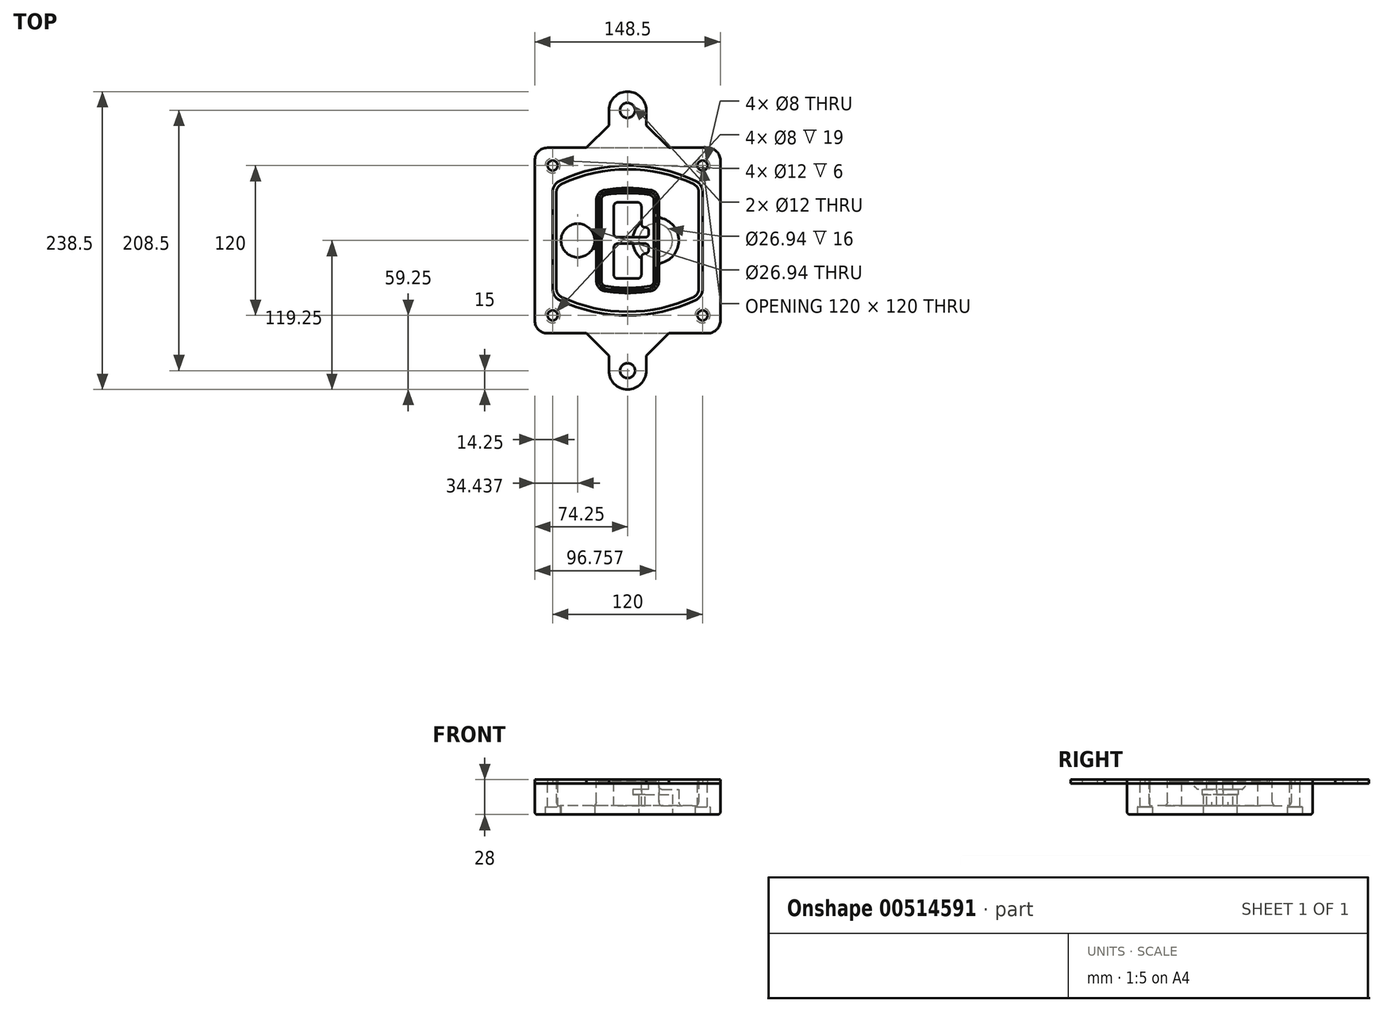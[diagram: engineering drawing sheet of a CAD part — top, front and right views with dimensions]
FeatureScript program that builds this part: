
annotation { "Feature Type Name" : "Feature", "Feature Type Description" : "" }
export const myFeature = defineFeature(function(context is Context, id is Id, definition is map)
    precondition{}
    {
        {
            var Q0;
            Q0=qCreatedBy(makeId("Top.planeOp"),FACE);
            var sketch = newSketch(context, id + "F0", { "sketchPlane" : qUnion([Q0])});
            skPoint(sketch, "E0.rect.middle", {"position": v(0, 0) * mm});
            skLineSegment(sketch, "E1.bottom", {"start": v(-64.25, -74.25) * mm, "end": v(64.25, -74.25) * mm});
            skLineSegment(sketch, "E1.top", {"start": v(-64.25, 74.25) * mm, "end": v(64.25, 74.25) * mm});
            skLineSegment(sketch, "E1.left", {"start": v(-74.25, -64.25) * mm, "end": v(-74.25, 64.25) * mm});
            skLineSegment(sketch, "E1.right", {"start": v(74.25, -64.25) * mm, "end": v(74.25, 64.25) * mm});
            skLineSegment(sketch, "E2", {"start": v(-74.25, 74.25) * mm, "end": v(74.25, -74.25) * mm, "construction": true});
            skLineSegment(sketch, "E3", {"start": v(74.25, 74.25) * mm, "end": v(-74.25, -74.25) * mm, "construction": true});
            skCircle(sketch, "E4", {"center": v(-60, 60) * mm, "radius": 4 * mm});
            skCircle(sketch, "E5", {"center": v(60, 60) * mm, "radius": 4 * mm});
            skCircle(sketch, "E6", {"center": v(60, -60) * mm, "radius": 4 * mm});
            skCircle(sketch, "E7", {"center": v(-60, -60) * mm, "radius": 4 * mm});
            skLineSegment(sketch, "E8", {"start": v(-60, 60) * mm, "end": v(60, 60) * mm, "construction": true});
            skLineSegment(sketch, "E9", {"start": v(60, 60) * mm, "end": v(60, -60) * mm, "construction": true});
            skLineSegment(sketch, "E10", {"start": v(60, -60) * mm, "end": v(-60, -60) * mm, "construction": true});
            skLineSegment(sketch, "E11", {"start": v(-60, -60) * mm, "end": v(-60, 60) * mm, "construction": true});
            skLineSegment(sketch, "E12", {"start": v(-60, 38.83) * mm, "end": v(-60, -38.83) * mm});
            skLineSegment(sketch, "E13", {"start": v(60, 38.83) * mm, "end": v(60, -38.83) * mm});
            skArc(sketch, "E14", {"start": v(54.26, 47.88) * mm, "mid": v(0, 60) * mm, "end": v(-54.26, 47.88) * mm});
            skArc(sketch, "E15", {"start": v(-54.26, -47.88) * mm, "mid": v(0, -60) * mm, "end": v(54.26, -47.88) * mm});
            skLineSegment(sketch, "E16", {"start": v(-60, 0) * mm, "end": v(60, 0) * mm, "construction": true});
            skPoint(sketch, "E17.visualSharp", {"position": v(-60, -45) * mm});
            skArc(sketch, "E17.filletArc", {"start": v(-60, -38.83) * mm, "mid": v(-58.44, -44.2) * mm, "end": v(-54.26, -47.88) * mm});
            skPoint(sketch, "E18.visualSharp", {"position": v(-60, 45) * mm});
            skArc(sketch, "E18.filletArc", {"start": v(-54.26, 47.88) * mm, "mid": v(-58.44, 44.2) * mm, "end": v(-60, 38.83) * mm});
            skPoint(sketch, "E19.visualSharp", {"position": v(60, 45) * mm});
            skArc(sketch, "E19.filletArc", {"start": v(60, 38.83) * mm, "mid": v(58.44, 44.2) * mm, "end": v(54.26, 47.88) * mm});
            skPoint(sketch, "E20.visualSharp", {"position": v(60, -45) * mm});
            skArc(sketch, "E20.filletArc", {"start": v(54.26, -47.88) * mm, "mid": v(58.44, -44.2) * mm, "end": v(60, -38.83) * mm});
            skPoint(sketch, "E21.visualSharp", {"position": v(-74.25, 74.25) * mm});
            skArc(sketch, "E21.filletArc", {"start": v(-64.25, 74.25) * mm, "mid": v(-71.32, 71.32) * mm, "end": v(-74.25, 64.25) * mm});
            skPoint(sketch, "E22.visualSharp", {"position": v(74.25, 74.25) * mm});
            skArc(sketch, "E22.filletArc", {"start": v(74.25, 64.25) * mm, "mid": v(71.32, 71.32) * mm, "end": v(64.25, 74.25) * mm});
            skPoint(sketch, "E23.visualSharp", {"position": v(74.25, -74.25) * mm});
            skArc(sketch, "E23.filletArc", {"start": v(64.25, -74.25) * mm, "mid": v(71.32, -71.32) * mm, "end": v(74.25, -64.25) * mm});
            skPoint(sketch, "E24.visualSharp", {"position": v(-74.25, -74.25) * mm});
            skArc(sketch, "E24.filletArc", {"start": v(-74.25, -64.25) * mm, "mid": v(-71.32, -71.32) * mm, "end": v(-64.25, -74.25) * mm});
            skArc(sketch, "E25.0", {"start": v(57, 38.83) * mm, "mid": v(55.9, 42.58) * mm, "end": v(52.98, 45.17) * mm});
            skLineSegment(sketch, "E25.1", {"start": v(57, 38.83) * mm, "end": v(57, -38.83) * mm});
            skArc(sketch, "E25.2", {"start": v(52.98, -45.17) * mm, "mid": v(55.9, -42.58) * mm, "end": v(57, -38.83) * mm});
            skArc(sketch, "E25.3", {"start": v(-52.98, -45.17) * mm, "mid": v(0, -57) * mm, "end": v(52.98, -45.17) * mm});
            skArc(sketch, "E25.4", {"start": v(-57, -38.83) * mm, "mid": v(-55.9, -42.58) * mm, "end": v(-52.98, -45.17) * mm});
            skArc(sketch, "E25.5", {"start": v(52.98, 45.17) * mm, "mid": v(0, 57) * mm, "end": v(-52.98, 45.17) * mm});
            skLineSegment(sketch, "E25.6", {"start": v(-57, 38.83) * mm, "end": v(-57, -38.83) * mm});
            skArc(sketch, "E25.7", {"start": v(-52.98, 45.17) * mm, "mid": v(-55.9, 42.58) * mm, "end": v(-57, 38.83) * mm});
            skArc(sketch, "E26.0", {"start": v(-55.96, 51.5) * mm, "mid": v(-61.82, 46.33) * mm, "end": v(-64, 38.83) * mm});
            skArc(sketch, "E26.1", {"start": v(55.96, 51.5) * mm, "mid": v(0, 64) * mm, "end": v(-55.96, 51.5) * mm});
            skArc(sketch, "E26.2", {"start": v(64, 38.83) * mm, "mid": v(61.82, 46.33) * mm, "end": v(55.96, 51.5) * mm});
            skLineSegment(sketch, "E26.3", {"start": v(64, 38.83) * mm, "end": v(64, -38.83) * mm});
            skArc(sketch, "E26.4", {"start": v(55.96, -51.5) * mm, "mid": v(61.82, -46.33) * mm, "end": v(64, -38.83) * mm});
            skLineSegment(sketch, "E26.5", {"start": v(-64, 38.83) * mm, "end": v(-64, -38.83) * mm});
            skArc(sketch, "E26.6", {"start": v(-55.96, -51.5) * mm, "mid": v(0, -64) * mm, "end": v(55.96, -51.5) * mm});
            skArc(sketch, "E26.7", {"start": v(-64, -38.83) * mm, "mid": v(-61.82, -46.33) * mm, "end": v(-55.96, -51.5) * mm});
            skSolve(sketch);
        }
        {
            var Q0;
            Q0=makeQuery(id+"F0.imprint","IMPRINT",FACE,{"disambiguationData":[TD([[makeQuery(id+"F0.imprint","IMPRINT",EDGE,{"derivedFrom":sQuery(id+"F0.wireOp",EDGE,"E1.bottom")}),1.0]])]});
            var Q1;
            Q1=makeQuery(id+"F0.imprint","IMPRINT",FACE,{"disambiguationData":[TD([[makeQuery(id+"F0.imprint","IMPRINT",EDGE,{"derivedFrom":sQuery(id+"F0.wireOp",EDGE,"E12")}),1.0]])]});
            var Q2;
            Q2=makeQuery(id+"F0.imprint","IMPRINT",FACE,{"disambiguationData":[TD([[makeQuery(id+"F0.imprint","IMPRINT",EDGE,{"derivedFrom":sQuery(id+"F0.wireOp",EDGE,"E25.0")}),1.0]])]});
            var Q3;
            Q3=makeQuery(id+"F0.imprint","IMPRINT",FACE,{"disambiguationData":[TD([[makeQuery(id+"F0.imprint","IMPRINT",EDGE,{"derivedFrom":sQuery(id+"F0.wireOp",EDGE,"E12")}),-1.0]])]});
            extrude(context, id + "F1", {"entities" : qUnion([Q0, Q1, Q2, Q3]), "oppositeDirection" : true, "depth" : 25 * mm});
        }
        {
            var Q0;
            Q0=makeQuery(id+"F0.imprint","IMPRINT",FACE,{"disambiguationData":[TD([[makeQuery(id+"F0.imprint","IMPRINT",EDGE,{"derivedFrom":sQuery(id+"F0.wireOp",EDGE,"E12")}),1.0]])]});
            extrude(context, id + "F2", {"entities" : qUnion([Q0]), "operationType" : NewBodyOperationType.ADD, "depth" : 3 * mm, "offsetDistance" : 25 * mm});
        }
        {
            var Q0;
            Q0=makeQuery(id+"F0.imprint","IMPRINT",FACE,{"disambiguationData":[TD([[makeQuery(id+"F0.imprint","IMPRINT",EDGE,{"derivedFrom":sQuery(id+"F0.wireOp",EDGE,"E25.0")}),1.0]])]});
            extrude(context, id + "F3", {"entities" : qUnion([Q0]), "operationType" : NewBodyOperationType.REMOVE, "oppositeDirection" : true, "depth" : 18 * mm});
        }
        {
            var Q0;
            Q0=makeQuery(id+"F2.opExtrude","CAP_FACE",FACE,{"disambiguationData":[OSD([sQuery(id+"F0.wireOp",EDGE,"E12"),sQuery(id+"F0.wireOp",EDGE,"E13"),sQuery(id+"F0.wireOp",EDGE,"E14"),sQuery(id+"F0.wireOp",EDGE,"E15"),sQuery(id+"F0.wireOp",EDGE,"E17.filletArc"),sQuery(id+"F0.wireOp",EDGE,"E18.filletArc"),sQuery(id+"F0.wireOp",EDGE,"E19.filletArc"),sQuery(id+"F0.wireOp",EDGE,"E20.filletArc"),sQuery(id+"F0.wireOp",EDGE,"E25.0"),sQuery(id+"F0.wireOp",EDGE,"E25.1"),sQuery(id+"F0.wireOp",EDGE,"E25.2"),sQuery(id+"F0.wireOp",EDGE,"E25.3"),sQuery(id+"F0.wireOp",EDGE,"E25.4"),sQuery(id+"F0.wireOp",EDGE,"E25.5"),sQuery(id+"F0.wireOp",EDGE,"E25.6"),sQuery(id+"F0.wireOp",EDGE,"E25.7")])],"isStart":false});
            var sketch = newSketch(context, id + "F4", { "sketchPlane" : qUnion([Q0])});
            skArc(sketch, "E27.0", {"start": v(-18.34, -40.45) * mm, "mid": v(0, -42) * mm, "end": v(18.34, -40.45) * mm});
            skArc(sketch, "E28.0", {"start": v(18.34, 40.45) * mm, "mid": v(0, 42) * mm, "end": v(-18.34, 40.45) * mm});
            skLineSegment(sketch, "E29", {"start": v(-25, 32.57) * mm, "end": v(-25, -32.57) * mm});
            skLineSegment(sketch, "E30", {"start": v(25, 32.57) * mm, "end": v(25, -32.57) * mm});
            skLineSegment(sketch, "E31", {"start": v(-25, 39.1) * mm, "end": v(25, 39.1) * mm, "construction": true});
            skLineSegment(sketch, "E32", {"start": v(-25, -39.1) * mm, "end": v(25, -39.1) * mm, "construction": true});
            skPoint(sketch, "E33.visualSharp", {"position": v(-25, 39.1) * mm});
            skArc(sketch, "E33.filletArc", {"start": v(-18.34, 40.45) * mm, "mid": v(-23.11, 37.73) * mm, "end": v(-25, 32.57) * mm});
            skPoint(sketch, "E34.visualSharp", {"position": v(25, 39.1) * mm});
            skArc(sketch, "E34.filletArc", {"start": v(25, 32.57) * mm, "mid": v(23.11, 37.73) * mm, "end": v(18.34, 40.45) * mm});
            skPoint(sketch, "E35.visualSharp", {"position": v(25, -39.1) * mm});
            skArc(sketch, "E35.filletArc", {"start": v(18.34, -40.45) * mm, "mid": v(23.11, -37.73) * mm, "end": v(25, -32.57) * mm});
            skPoint(sketch, "E36.visualSharp", {"position": v(-25, -39.1) * mm});
            skArc(sketch, "E36.filletArc", {"start": v(-25, -32.57) * mm, "mid": v(-23.11, -37.73) * mm, "end": v(-18.34, -40.45) * mm});
            skArc(sketch, "E37.0", {"start": v(52.98, 45.17) * mm, "mid": v(0, 57) * mm, "end": v(-52.98, 45.17) * mm});
            skArc(sketch, "E37.1", {"start": v(-52.98, 45.17) * mm, "mid": v(-55.9, 42.58) * mm, "end": v(-57, 38.83) * mm});
            skLineSegment(sketch, "E37.2", {"start": v(-57, 38.83) * mm, "end": v(-57, -38.83) * mm});
            skArc(sketch, "E37.3", {"start": v(-57, -38.83) * mm, "mid": v(-55.9, -42.58) * mm, "end": v(-52.98, -45.17) * mm});
            skArc(sketch, "E37.4", {"start": v(-52.98, -45.17) * mm, "mid": v(0, -57) * mm, "end": v(52.98, -45.17) * mm});
            skArc(sketch, "E37.5", {"start": v(52.98, -45.17) * mm, "mid": v(55.9, -42.58) * mm, "end": v(57, -38.83) * mm});
            skLineSegment(sketch, "E37.6", {"start": v(57, 38.83) * mm, "end": v(57, -38.83) * mm});
            skArc(sketch, "E37.7", {"start": v(57, 38.83) * mm, "mid": v(55.9, 42.58) * mm, "end": v(52.98, 45.17) * mm});
            skLineSegment(sketch, "E38.0", {"start": v(23, 32.57) * mm, "end": v(23, -32.57) * mm});
            skArc(sketch, "E38.1", {"start": v(18, -38.48) * mm, "mid": v(21.58, -36.44) * mm, "end": v(23, -32.57) * mm});
            skArc(sketch, "E38.2", {"start": v(-18, -38.48) * mm, "mid": v(0, -40) * mm, "end": v(18, -38.48) * mm});
            skArc(sketch, "E38.3", {"start": v(-23, -32.57) * mm, "mid": v(-21.58, -36.44) * mm, "end": v(-18, -38.48) * mm});
            skLineSegment(sketch, "E38.4", {"start": v(-23, 32.57) * mm, "end": v(-23, -32.57) * mm});
            skArc(sketch, "E38.5", {"start": v(23, 32.57) * mm, "mid": v(21.58, 36.44) * mm, "end": v(18, 38.48) * mm});
            skArc(sketch, "E38.6", {"start": v(-18, 38.48) * mm, "mid": v(-21.58, 36.44) * mm, "end": v(-23, 32.57) * mm});
            skArc(sketch, "E38.7", {"start": v(18, 38.48) * mm, "mid": v(0, 40) * mm, "end": v(-18, 38.48) * mm});
            skArc(sketch, "E39.0", {"start": v(21, 32.57) * mm, "mid": v(20.06, 35.15) * mm, "end": v(17.67, 36.5) * mm});
            skLineSegment(sketch, "E39.1", {"start": v(21, 32.57) * mm, "end": v(21, -32.57) * mm});
            skArc(sketch, "E39.2", {"start": v(17.67, -36.5) * mm, "mid": v(20.06, -35.15) * mm, "end": v(21, -32.57) * mm});
            skArc(sketch, "E39.3", {"start": v(-17.67, -36.5) * mm, "mid": v(0, -38) * mm, "end": v(17.67, -36.5) * mm});
            skArc(sketch, "E39.4", {"start": v(-21, -32.57) * mm, "mid": v(-20.06, -35.15) * mm, "end": v(-17.67, -36.5) * mm});
            skArc(sketch, "E39.5", {"start": v(17.67, 36.5) * mm, "mid": v(0, 38) * mm, "end": v(-17.67, 36.5) * mm});
            skLineSegment(sketch, "E39.6", {"start": v(-21, 32.57) * mm, "end": v(-21, -32.57) * mm});
            skArc(sketch, "E39.7", {"start": v(-17.67, 36.5) * mm, "mid": v(-20.06, 35.15) * mm, "end": v(-21, 32.57) * mm});
            skLineSegment(sketch, "E40", {"start": v(-25, 0) * mm, "end": v(25, 0) * mm, "construction": true});
            skLineSegment(sketch, "E41", {"start": v(-11, 5.5) * mm, "end": v(-11, 27.5) * mm});
            skLineSegment(sketch, "E42", {"start": v(-8, 30.5) * mm, "end": v(8, 30.5) * mm});
            skLineSegment(sketch, "E43", {"start": v(11, 27.5) * mm, "end": v(11, 13.5) * mm});
            skLineSegment(sketch, "E44", {"start": v(14, 10.5) * mm, "end": v(14, 10.5) * mm});
            skLineSegment(sketch, "E45", {"start": v(17, 7.5) * mm, "end": v(17, 5.5) * mm});
            skLineSegment(sketch, "E46", {"start": v(14, 2.5) * mm, "end": v(-8, 2.5) * mm});
            skPoint(sketch, "E47.visualSharp", {"position": v(-11, 30.5) * mm});
            skArc(sketch, "E47.filletArc", {"start": v(-8, 30.5) * mm, "mid": v(-10.12, 29.62) * mm, "end": v(-11, 27.5) * mm});
            skPoint(sketch, "E48.visualSharp", {"position": v(11, 30.5) * mm});
            skArc(sketch, "E48.filletArc", {"start": v(11, 27.5) * mm, "mid": v(10.12, 29.62) * mm, "end": v(8, 30.5) * mm});
            skPoint(sketch, "E49.visualSharp", {"position": v(11, 10.5) * mm});
            skArc(sketch, "E49.filletArc", {"start": v(11, 13.5) * mm, "mid": v(11.88, 11.38) * mm, "end": v(14, 10.5) * mm});
            skPoint(sketch, "E50.visualSharp", {"position": v(17, 10.5) * mm});
            skArc(sketch, "E50.filletArc", {"start": v(17, 7.5) * mm, "mid": v(16.12, 9.62) * mm, "end": v(14, 10.5) * mm});
            skPoint(sketch, "E51.visualSharp", {"position": v(17, 2.5) * mm});
            skArc(sketch, "E51.filletArc", {"start": v(14, 2.5) * mm, "mid": v(16.12, 3.38) * mm, "end": v(17, 5.5) * mm});
            skPoint(sketch, "E52.visualSharp", {"position": v(-11, 2.5) * mm});
            skArc(sketch, "E52.filletArc", {"start": v(-11, 5.5) * mm, "mid": v(-10.12, 3.38) * mm, "end": v(-8, 2.5) * mm});
            skLineSegment(sketch, "E53.0.MirrorCS", {"start": v(14, -2.5) * mm, "end": v(-8, -2.5) * mm});
            skArc(sketch, "E54.0.MirrorCS", {"start": v(-11, -5.5) * mm, "mid": v(-10.12, -3.38) * mm, "end": v(-8, -2.5) * mm});
            skLineSegment(sketch, "E55.0.MirrorCS", {"start": v(-11, -5.5) * mm, "end": v(-11, -27.5) * mm});
            skArc(sketch, "E56.0.MirrorCS", {"start": v(-8, -30.5) * mm, "mid": v(-10.12, -29.62) * mm, "end": v(-11, -27.5) * mm});
            skLineSegment(sketch, "E57.0.MirrorCS", {"start": v(-8, -30.5) * mm, "end": v(8, -30.5) * mm});
            skArc(sketch, "E58.0.MirrorCS", {"start": v(11, -27.5) * mm, "mid": v(10.12, -29.62) * mm, "end": v(8, -30.5) * mm});
            skLineSegment(sketch, "E59.0.MirrorCS", {"start": v(11, -27.5) * mm, "end": v(11, -13.5) * mm});
            skArc(sketch, "E60.0.MirrorCS", {"start": v(11, -13.5) * mm, "mid": v(11.88, -11.38) * mm, "end": v(14, -10.5) * mm});
            skArc(sketch, "E61.0.MirrorCS", {"start": v(17, -7.5) * mm, "mid": v(16.12, -9.62) * mm, "end": v(14, -10.5) * mm});
            skLineSegment(sketch, "E62.0.MirrorCS", {"start": v(17, -7.5) * mm, "end": v(17, -5.5) * mm});
            skArc(sketch, "E63.0.MirrorCS", {"start": v(14, -2.5) * mm, "mid": v(16.12, -3.38) * mm, "end": v(17, -5.5) * mm});
            skSolve(sketch);
        }
        {
            var Q0;
            Q0=makeQuery(id+"F4.imprint","IMPRINT",FACE,{"disambiguationData":[TD([[makeQuery(id+"F4.imprint","IMPRINT",EDGE,{"derivedFrom":sQuery(id+"F4.wireOp",EDGE,"E27.0")}),1.0]])]});
            var Q1;
            Q1=makeQuery(id+"F4.imprint","IMPRINT",FACE,{"disambiguationData":[TD([[makeQuery(id+"F4.imprint","IMPRINT",EDGE,{"derivedFrom":sQuery(id+"F4.wireOp",EDGE,"E38.0")}),-1.0]])]});
            var Q2;
            Q2=makeQuery(id+"F4.imprint","IMPRINT",FACE,{"disambiguationData":[TD([[makeQuery(id+"F4.imprint","IMPRINT",EDGE,{"derivedFrom":sQuery(id+"F4.wireOp",EDGE,"E39.0")}),1.0]])]});
            extrude(context, id + "F5", {"entities" : qUnion([Q0, Q1, Q2]), "operationType" : NewBodyOperationType.ADD, "endBound" : BoundingType.UP_TO_NEXT, "oppositeDirection" : true, "depth" : 25 * mm});
        }
        {
            var Q0;
            Q0=makeQuery(id+"F4.imprint","IMPRINT",FACE,{"disambiguationData":[TD([[makeQuery(id+"F4.imprint","IMPRINT",EDGE,{"derivedFrom":sQuery(id+"F4.wireOp",EDGE,"E38.0")}),-1.0]])]});
            extrude(context, id + "F6", {"entities" : qUnion([Q0]), "operationType" : NewBodyOperationType.REMOVE, "oppositeDirection" : true, "depth" : 2 * mm});
        }
        {
            var Q0;
            Q0=makeQuery(id+"F1.opExtrude","CAP_FACE",FACE,{"disambiguationData":[OSD([sQuery(id+"F0.wireOp",EDGE,"E1.bottom"),sQuery(id+"F0.wireOp",EDGE,"E1.top"),sQuery(id+"F0.wireOp",EDGE,"E1.left"),sQuery(id+"F0.wireOp",EDGE,"E1.right"),sQuery(id+"F0.wireOp",EDGE,"E4"),sQuery(id+"F0.wireOp",EDGE,"E5"),sQuery(id+"F0.wireOp",EDGE,"E6"),sQuery(id+"F0.wireOp",EDGE,"E7"),sQuery(id+"F0.wireOp",EDGE,"E21.filletArc"),sQuery(id+"F0.wireOp",EDGE,"E22.filletArc"),sQuery(id+"F0.wireOp",EDGE,"E23.filletArc"),sQuery(id+"F0.wireOp",EDGE,"E24.filletArc")])],"isStart":false});
            var sketch = newSketch(context, id + "F7", { "sketchPlane" : qUnion([Q0])});
            skCircle(sketch, "E64", {"center": v(22.5, 0) * mm, "radius": 13.47 * mm});
            skCircle(sketch, "E65", {"center": v(-39.81, 0) * mm, "radius": 13.47 * mm});
            skLineSegment(sketch, "E66", {"start": v(74.25, 0) * mm, "end": v(-74.25, 0) * mm});
            skCircle(sketch, "E67", {"center": v(22.5, 0) * mm, "radius": 18.47 * mm});
            skCircle(sketch, "E68", {"center": v(60, -60) * mm, "radius": 6 * mm});
            skCircle(sketch, "E69", {"center": v(-60, -60) * mm, "radius": 6 * mm});
            skCircle(sketch, "E70", {"center": v(-60, 60) * mm, "radius": 6 * mm});
            skCircle(sketch, "E71", {"center": v(60, 60) * mm, "radius": 6 * mm});
            skSolve(sketch);
        }
        {
            var Q0;
            {var subQ1=sQuery(id+"F7.wireOp",EDGE,"E66");var subQ4=sQuery(id+"F7.wireOp",EDGE,"E64");var subQ6=makeQuery(id+"F7.imprint","INTERSECT",VERTEX,{"disambiguationData":[OD(0.0)],"derivedFrom":[subQ4,subQ1]});Q0=makeQuery(id+"F7.imprint","IMPRINT",FACE,{"disambiguationData":[TD([[makeQuery(id+"F7.imprint","IMPRINT",EDGE,{"disambiguationData":[TD([[subQ6,-1.0]])],"derivedFrom":subQ4}),-1.0]])]});}
            var Q1;
            {var subQ0=sQuery(id+"F7.wireOp",EDGE,"E66");var subQ1=sQuery(id+"F7.wireOp",EDGE,"E64");var subQ3=makeQuery(id+"F7.imprint","INTERSECT",VERTEX,{"disambiguationData":[OD(0.0)],"derivedFrom":[subQ1,subQ0]});Q1=makeQuery(id+"F7.imprint","IMPRINT",FACE,{"disambiguationData":[TD([[makeQuery(id+"F7.imprint","IMPRINT",EDGE,{"disambiguationData":[TD([[subQ3,-1.0]])],"derivedFrom":subQ1}),1.0]])]});}
            var Q2;
            {var subQ0=sQuery(id+"F7.wireOp",EDGE,"E66");var subQ1=sQuery(id+"F7.wireOp",EDGE,"E64");var subQ3=makeQuery(id+"F7.imprint","INTERSECT",VERTEX,{"disambiguationData":[OD(0.0)],"derivedFrom":[subQ1,subQ0]});Q2=makeQuery(id+"F7.imprint","IMPRINT",FACE,{"disambiguationData":[TD([[makeQuery(id+"F7.imprint","IMPRINT",EDGE,{"disambiguationData":[TD([[subQ3,1.0]])],"derivedFrom":subQ1}),1.0]])]});}
            var Q3;
            {var subQ1=sQuery(id+"F7.wireOp",EDGE,"E66");var subQ4=sQuery(id+"F7.wireOp",EDGE,"E64");var subQ6=makeQuery(id+"F7.imprint","INTERSECT",VERTEX,{"disambiguationData":[OD(0.0)],"derivedFrom":[subQ4,subQ1]});Q3=makeQuery(id+"F7.imprint","IMPRINT",FACE,{"disambiguationData":[TD([[makeQuery(id+"F7.imprint","IMPRINT",EDGE,{"disambiguationData":[TD([[subQ6,1.0]])],"derivedFrom":subQ4}),-1.0]])]});}
            extrude(context, id + "F8", {"entities" : qUnion([Q0, Q1, Q2, Q3]), "operationType" : NewBodyOperationType.ADD, "oppositeDirection" : true, "depth" : 20 * mm});
        }
        {
            var Q0;
            {var subQ0=sQuery(id+"F7.wireOp",EDGE,"E66");var subQ1=sQuery(id+"F7.wireOp",EDGE,"E64");var subQ3=makeQuery(id+"F7.imprint","INTERSECT",VERTEX,{"disambiguationData":[OD(0.0)],"derivedFrom":[subQ1,subQ0]});Q0=makeQuery(id+"F7.imprint","IMPRINT",FACE,{"disambiguationData":[TD([[makeQuery(id+"F7.imprint","IMPRINT",EDGE,{"disambiguationData":[TD([[subQ3,-1.0]])],"derivedFrom":subQ1}),1.0]])]});}
            var Q1;
            {var subQ0=sQuery(id+"F7.wireOp",EDGE,"E66");var subQ1=sQuery(id+"F7.wireOp",EDGE,"E64");var subQ3=makeQuery(id+"F7.imprint","INTERSECT",VERTEX,{"disambiguationData":[OD(0.0)],"derivedFrom":[subQ1,subQ0]});Q1=makeQuery(id+"F7.imprint","IMPRINT",FACE,{"disambiguationData":[TD([[makeQuery(id+"F7.imprint","IMPRINT",EDGE,{"disambiguationData":[TD([[subQ3,1.0]])],"derivedFrom":subQ1}),1.0]])]});}
            extrude(context, id + "F9", {"entities" : qUnion([Q0, Q1]), "operationType" : NewBodyOperationType.REMOVE, "oppositeDirection" : true, "depth" : 16 * mm});
        }
        {
            var Q0;
            {var subQ0=sQuery(id+"F7.wireOp",EDGE,"E66");var subQ1=sQuery(id+"F7.wireOp",EDGE,"E65");var subQ3=makeQuery(id+"F7.imprint","INTERSECT",VERTEX,{"disambiguationData":[OD(0.0)],"derivedFrom":[subQ1,subQ0]});Q0=makeQuery(id+"F7.imprint","IMPRINT",FACE,{"disambiguationData":[TD([[makeQuery(id+"F7.imprint","IMPRINT",EDGE,{"disambiguationData":[TD([[subQ3,-1.0]])],"derivedFrom":subQ1}),1.0]])]});}
            var Q1;
            {var subQ0=sQuery(id+"F7.wireOp",EDGE,"E66");var subQ1=sQuery(id+"F7.wireOp",EDGE,"E65");var subQ3=makeQuery(id+"F7.imprint","INTERSECT",VERTEX,{"disambiguationData":[OD(0.0)],"derivedFrom":[subQ1,subQ0]});Q1=makeQuery(id+"F7.imprint","IMPRINT",FACE,{"disambiguationData":[TD([[makeQuery(id+"F7.imprint","IMPRINT",EDGE,{"disambiguationData":[TD([[subQ3,1.0]])],"derivedFrom":subQ1}),1.0]])]});}
            extrude(context, id + "F10", {"entities" : qUnion([Q0, Q1]), "operationType" : NewBodyOperationType.REMOVE, "oppositeDirection" : true, "depth" : 25 * mm});
        }
        {
            var Q0;
            Q0=makeQuery(id+"F7.imprint","IMPRINT",FACE,{"disambiguationData":[TD([[makeQuery(id+"F7.imprint","IMPRINT",EDGE,{"derivedFrom":sQuery(id+"F7.wireOp",EDGE,"E68")}),1.0]])]});
            var Q1;
            Q1=makeQuery(id+"F7.imprint","IMPRINT",FACE,{"disambiguationData":[TD([[makeQuery(id+"F7.imprint","IMPRINT",EDGE,{"derivedFrom":makeQuery(id+"F1.opExtrude","CAP_EDGE",EDGE,{"disambiguationData":[OSD([sQuery(id+"F0.wireOp",EDGE,"E5")])],"isStart":false})}),-1.0]])]});
            var Q2;
            Q2=makeQuery(id+"F7.imprint","IMPRINT",FACE,{"disambiguationData":[TD([[makeQuery(id+"F7.imprint","IMPRINT",EDGE,{"derivedFrom":sQuery(id+"F7.wireOp",EDGE,"E69")}),1.0]])]});
            var Q3;
            Q3=makeQuery(id+"F7.imprint","IMPRINT",FACE,{"disambiguationData":[TD([[makeQuery(id+"F7.imprint","IMPRINT",EDGE,{"derivedFrom":makeQuery(id+"F1.opExtrude","CAP_EDGE",EDGE,{"disambiguationData":[OSD([sQuery(id+"F0.wireOp",EDGE,"E4")])],"isStart":false})}),-1.0]])]});
            var Q4;
            Q4=makeQuery(id+"F7.imprint","IMPRINT",FACE,{"disambiguationData":[TD([[makeQuery(id+"F7.imprint","IMPRINT",EDGE,{"derivedFrom":sQuery(id+"F7.wireOp",EDGE,"E70")}),1.0]])]});
            var Q5;
            Q5=makeQuery(id+"F7.imprint","IMPRINT",FACE,{"disambiguationData":[TD([[makeQuery(id+"F7.imprint","IMPRINT",EDGE,{"derivedFrom":makeQuery(id+"F1.opExtrude","CAP_EDGE",EDGE,{"disambiguationData":[OSD([sQuery(id+"F0.wireOp",EDGE,"E7")])],"isStart":false})}),-1.0]])]});
            var Q6;
            Q6=makeQuery(id+"F7.imprint","IMPRINT",FACE,{"disambiguationData":[TD([[makeQuery(id+"F7.imprint","IMPRINT",EDGE,{"derivedFrom":sQuery(id+"F7.wireOp",EDGE,"E71")}),1.0]])]});
            var Q7;
            Q7=makeQuery(id+"F7.imprint","IMPRINT",FACE,{"disambiguationData":[TD([[makeQuery(id+"F7.imprint","IMPRINT",EDGE,{"derivedFrom":makeQuery(id+"F1.opExtrude","CAP_EDGE",EDGE,{"disambiguationData":[OSD([sQuery(id+"F0.wireOp",EDGE,"E6")])],"isStart":false})}),-1.0]])]});
            extrude(context, id + "F11", {"entities" : qUnion([Q0, Q1, Q2, Q3, Q4, Q5, Q6, Q7]), "operationType" : NewBodyOperationType.REMOVE, "oppositeDirection" : true, "depth" : 6 * mm});
        }
        {
            var Q0;
            Q0=makeQuery(id+"F9.boolean.opBoolean","COPY",FACE,{"derivedFrom":makeQuery(id+"F9.opExtrude","CAP_FACE",FACE,{"disambiguationData":[OSD([sQuery(id+"F7.wireOp",EDGE,"E64")])],"isStart":false})});
            var sketch = newSketch(context, id + "F12", { "sketchPlane" : qUnion([Q0])});
            skArc(sketch, "E72.0", {"start": v(11, 14.45) * mm, "mid": v(6.45, 9.13) * mm, "end": v(4.2, 2.5) * mm});
            skArc(sketch, "E72.1", {"start": v(4.2, -2.5) * mm, "mid": v(6.45, -9.13) * mm, "end": v(11, -14.45) * mm});
            skLineSegment(sketch, "E73", {"start": v(4.2, -2.5) * mm, "end": v(14, -2.5) * mm});
            skLineSegment(sketch, "E74.0", {"start": v(14, 2.5) * mm, "end": v(4.2, 2.5) * mm});
            skArc(sketch, "E74.1", {"start": v(14, 2.5) * mm, "mid": v(16.12, 3.38) * mm, "end": v(17, 5.5) * mm});
            skLineSegment(sketch, "E74.2", {"start": v(17, 7.5) * mm, "end": v(17, 5.5) * mm});
            skArc(sketch, "E74.3", {"start": v(17, 7.5) * mm, "mid": v(16.12, 9.62) * mm, "end": v(14, 10.5) * mm});
            skArc(sketch, "E74.4", {"start": v(11, 13.5) * mm, "mid": v(11.88, 11.38) * mm, "end": v(14, 10.5) * mm});
            skLineSegment(sketch, "E74.5", {"start": v(11, 14.45) * mm, "end": v(11, 13.5) * mm});
            skLineSegment(sketch, "E74.7", {"start": v(14, -2.5) * mm, "end": v(4.2, -2.5) * mm});
            skArc(sketch, "E74.8", {"start": v(14, -2.5) * mm, "mid": v(16.12, -3.38) * mm, "end": v(17, -5.5) * mm});
            skLineSegment(sketch, "E74.9", {"start": v(17, -7.5) * mm, "end": v(17, -5.5) * mm});
            skArc(sketch, "E74.10", {"start": v(17, -7.5) * mm, "mid": v(16.12, -9.62) * mm, "end": v(14, -10.5) * mm});
            skArc(sketch, "E74.11", {"start": v(11, -13.5) * mm, "mid": v(11.88, -11.38) * mm, "end": v(14, -10.5) * mm});
            skLineSegment(sketch, "E74.12", {"start": v(11, -14.45) * mm, "end": v(11, -13.5) * mm});
            skPoint(sketch, "E75.orphan", {"position": v(11, -27.5) * mm});
            skPoint(sketch, "E76.orphan", {"position": v(-8, -2.5) * mm});
            skPoint(sketch, "E77.orphan", {"position": v(-8, 2.5) * mm});
            skPoint(sketch, "E78.orphan", {"position": v(11, 27.5) * mm});
            skSolve(sketch);
        }
        {
            var Q0;
            {var subQ7=sQuery(id+"F12.wireOp",EDGE,"E72.0");var subQ14=sQuery(id+"F12.wireOp",EDGE,"E72.1");var subQ16=sQuery(id+"F12.wireOp",EDGE,"E74.1");var subQ18=sQuery(id+"F12.wireOp",EDGE,"E74.8");Q0=qUnion([makeQuery(id+"F12.imprint","IMPRINT",FACE,{"disambiguationData":[TD([[makeQuery(id+"F12.imprint","IMPRINT",EDGE,{"derivedFrom":subQ7}),1.0]])]}),makeQuery(id+"F12.imprint","IMPRINT",FACE,{"disambiguationData":[TD([[makeQuery(id+"F12.imprint","IMPRINT",EDGE,{"derivedFrom":subQ14}),1.0]])]}),makeQuery(id+"F12.imprint","IMPRINT",FACE,{"disambiguationData":[TD([[makeQuery(id+"F12.imprint","IMPRINT",EDGE,{"derivedFrom":subQ16}),1.0]])]}),makeQuery(id+"F12.imprint","IMPRINT",FACE,{"disambiguationData":[TD([[makeQuery(id+"F12.imprint","IMPRINT",EDGE,{"derivedFrom":subQ18}),-1.0]])]})]);}
            var Q1;
            Q1=makeQuery(id+"F5.boolean.opBoolean","SPLIT",FACE,{"disambiguationData":[TD([makeQuery(id+"F5.opExtrude","SWEPT_FACE",FACE,{"disambiguationData":[OSD([sQuery(id+"F4.wireOp",EDGE,"E41")])]})])],"derivedFrom":makeQuery(id+"F3.boolean.opBoolean","COPY",FACE,{"derivedFrom":makeQuery(id+"F3.opExtrude","CAP_FACE",FACE,{"disambiguationData":[OSD([sQuery(id+"F0.wireOp",EDGE,"E25.0"),sQuery(id+"F0.wireOp",EDGE,"E25.1"),sQuery(id+"F0.wireOp",EDGE,"E25.2"),sQuery(id+"F0.wireOp",EDGE,"E25.3"),sQuery(id+"F0.wireOp",EDGE,"E25.4"),sQuery(id+"F0.wireOp",EDGE,"E25.5"),sQuery(id+"F0.wireOp",EDGE,"E25.6"),sQuery(id+"F0.wireOp",EDGE,"E25.7")])],"isStart":false})})});
            extrude(context, id + "F13", {"entities" : qUnion([Q0]), "operationType" : NewBodyOperationType.REMOVE, "endBound" : BoundingType.UP_TO_SURFACE, "endBoundEntityFace" : qUnion([Q1]), "depth" : 25 * mm});
        }
        {
            var Q0;
            Q0=makeQuery(id+"F3.boolean.opBoolean","COPY",EDGE,{"derivedFrom":makeQuery(id+"F3.opExtrude","CAP_EDGE",EDGE,{"disambiguationData":[OSD([sQuery(id+"F0.wireOp",EDGE,"E25.6")])],"isStart":false})});
            var Q1;
            Q1=makeQuery(id+"F8.boolean.opBoolean","INTERSECT",EDGE,{"derivedFrom":[makeQuery(id+"F5.opExtrude","SWEPT_FACE",FACE,{"disambiguationData":[OSD([sQuery(id+"F4.wireOp",EDGE,"E30")])]}),makeQuery(id+"F8.opExtrude","CAP_FACE",FACE,{"disambiguationData":[OSD([sQuery(id+"F7.wireOp",EDGE,"E67")])],"isStart":false})]});
            var Q2;
            Q2=makeQuery(id+"F8.boolean.opBoolean","INTERSECT",EDGE,{"disambiguationData":[OD(1.0)],"derivedFrom":[makeQuery(id+"F5.opExtrude","SWEPT_FACE",FACE,{"disambiguationData":[OSD([sQuery(id+"F4.wireOp",EDGE,"E30")])]}),makeQuery(id+"F8.opExtrude","SWEPT_FACE",FACE,{"disambiguationData":[OSD([sQuery(id+"F7.wireOp",EDGE,"E67")])]})]});
            var Q3;
            {var subQ0=sQuery(id+"F4.wireOp",EDGE,"E30");Q3=makeQuery(id+"F8.boolean.opBoolean","SPLIT",EDGE,{"disambiguationData":[TD([makeQuery(id+"F5.opExtrude","SWEPT_FACE",FACE,{"disambiguationData":[OSD([sQuery(id+"F4.wireOp",EDGE,"E35.filletArc")])]})])],"derivedFrom":makeQuery(id+"F5.opExtrude","CAP_EDGE",EDGE,{"disambiguationData":[OSD([subQ0])],"isStart":false})});}
            var Q4;
            {var subQ0=sQuery(id+"F0.wireOp",EDGE,"E25.7");var subQ1=sQuery(id+"F0.wireOp",EDGE,"E25.1");var subQ2=sQuery(id+"F0.wireOp",EDGE,"E25.6");var subQ3=sQuery(id+"F0.wireOp",EDGE,"E25.5");var subQ4=sQuery(id+"F0.wireOp",EDGE,"E25.4");var subQ5=sQuery(id+"F0.wireOp",EDGE,"E25.0");var subQ6=sQuery(id+"F0.wireOp",EDGE,"E25.2");var subQ7=sQuery(id+"F0.wireOp",EDGE,"E25.3");Q4=makeQuery(id+"F8.boolean.opBoolean","INTERSECT",EDGE,{"derivedFrom":[makeQuery(id+"F5.boolean.opBoolean","SPLIT",FACE,{"disambiguationData":[TD([makeQuery(id+"F2.opExtrude","SWEPT_FACE",FACE,{"disambiguationData":[OSD([subQ5])]})])],"derivedFrom":makeQuery(id+"F3.boolean.opBoolean","COPY",FACE,{"derivedFrom":makeQuery(id+"F3.opExtrude","CAP_FACE",FACE,{"disambiguationData":[OSD([subQ5,subQ1,subQ6,subQ7,subQ4,subQ3,subQ2,subQ0])],"isStart":false})})}),makeQuery(id+"F8.opExtrude","SWEPT_FACE",FACE,{"disambiguationData":[OSD([sQuery(id+"F7.wireOp",EDGE,"E67")])]})]});}
            var Q5;
            Q5=makeQuery(id+"F8.boolean.opBoolean","INTERSECT",EDGE,{"disambiguationData":[OD(0.0)],"derivedFrom":[makeQuery(id+"F5.opExtrude","SWEPT_FACE",FACE,{"disambiguationData":[OSD([sQuery(id+"F4.wireOp",EDGE,"E30")])]}),makeQuery(id+"F8.opExtrude","SWEPT_FACE",FACE,{"disambiguationData":[OSD([sQuery(id+"F7.wireOp",EDGE,"E67")])]})]});
            fillet(context, id + "F14", {"entities" : qUnion([Q0, Q1, Q2, Q3, Q4, Q5]), "radius" : 3 * mm, "tangentPropagation" : true, "allowEdgeOverflow" : false});
        }
        {
            var Q0;
            Q0=makeQuery(id+"F1.opExtrude","CAP_EDGE",EDGE,{"disambiguationData":[OSD([sQuery(id+"F0.wireOp",EDGE,"E1.bottom")])],"isStart":false});
            fillet(context, id + "F15", {"entities" : qUnion([Q0]), "radius" : 2 * mm, "tangentPropagation" : true, "allowEdgeOverflow" : false});
        }
        {
            var Q0;
            {var subQ0=sQuery(id+"F0.wireOp",EDGE,"E21.filletArc");var subQ1=sQuery(id+"F0.wireOp",EDGE,"E7");var subQ2=sQuery(id+"F0.wireOp",EDGE,"E6");var subQ3=sQuery(id+"F0.wireOp",EDGE,"E5");var subQ4=sQuery(id+"F0.wireOp",EDGE,"E4");var subQ5=sQuery(id+"F0.wireOp",EDGE,"E22.filletArc");var subQ6=sQuery(id+"F0.wireOp",EDGE,"E1.bottom");var subQ7=sQuery(id+"F0.wireOp",EDGE,"E1.right");var subQ8=sQuery(id+"F0.wireOp",EDGE,"E1.top");var subQ9=sQuery(id+"F0.wireOp",EDGE,"E1.left");var subQ10=sQuery(id+"F0.wireOp",EDGE,"E23.filletArc");var subQ11=sQuery(id+"F0.wireOp",EDGE,"E24.filletArc");Q0=makeQuery(id+"F2.boolean.opBoolean","SPLIT",FACE,{"disambiguationData":[TD([makeQuery(id+"F1.opExtrude","SWEPT_FACE",FACE,{"disambiguationData":[OSD([subQ6])]})])],"derivedFrom":makeQuery(id+"F1.opExtrude","CAP_FACE",FACE,{"disambiguationData":[OSD([subQ6,subQ8,subQ9,subQ7,subQ4,subQ3,subQ2,subQ1,subQ0,subQ5,subQ10,subQ11])],"isStart":true})});}
            var sketch = newSketch(context, id + "F16", { "sketchPlane" : qUnion([Q0])});
            skArc(sketch, "E79.0", {"start": v(-64.25, 74.25) * mm, "mid": v(-71.32, 71.32) * mm, "end": v(-74.25, 64.25) * mm});
            skArc(sketch, "E79.1", {"start": v(74.25, 64.25) * mm, "mid": v(71.32, 71.32) * mm, "end": v(64.25, 74.25) * mm});
            skArc(sketch, "E79.2", {"start": v(60, 38.83) * mm, "mid": v(58.44, 44.2) * mm, "end": v(54.26, 47.88) * mm});
            skArc(sketch, "E79.3", {"start": v(-54.26, 47.88) * mm, "mid": v(-58.44, 44.2) * mm, "end": v(-60, 38.83) * mm});
            skArc(sketch, "E79.4", {"start": v(54.26, -47.88) * mm, "mid": v(58.44, -44.2) * mm, "end": v(60, -38.83) * mm});
            skArc(sketch, "E79.5", {"start": v(-60, -38.83) * mm, "mid": v(-58.44, -44.2) * mm, "end": v(-54.26, -47.88) * mm});
            skArc(sketch, "E79.6", {"start": v(64.25, -74.25) * mm, "mid": v(71.32, -71.32) * mm, "end": v(74.25, -64.25) * mm});
            skLineSegment(sketch, "E79.7", {"start": v(74.25, -64.25) * mm, "end": v(74.25, 64.25) * mm});
            skLineSegment(sketch, "E79.8", {"start": v(-64.25, 74.25) * mm, "end": v(64.25, 74.25) * mm});
            skLineSegment(sketch, "E79.9", {"start": v(-74.25, -64.25) * mm, "end": v(-74.25, 64.25) * mm});
            skArc(sketch, "E79.10", {"start": v(-74.25, -64.25) * mm, "mid": v(-71.32, -71.32) * mm, "end": v(-64.25, -74.25) * mm});
            skLineSegment(sketch, "E79.11", {"start": v(-64.25, -74.25) * mm, "end": v(64.25, -74.25) * mm});
            skLineSegment(sketch, "E79.12", {"start": v(60, 38.83) * mm, "end": v(60, -38.83) * mm});
            skArc(sketch, "E79.13", {"start": v(54.26, 47.88) * mm, "mid": v(0, 60) * mm, "end": v(-54.26, 47.88) * mm});
            skLineSegment(sketch, "E79.14", {"start": v(-60, 38.83) * mm, "end": v(-60, -38.83) * mm});
            skArc(sketch, "E79.15", {"start": v(-54.26, -47.88) * mm, "mid": v(0, -60) * mm, "end": v(54.26, -47.88) * mm});
            skCircle(sketch, "E79.16", {"center": v(60, 60) * mm, "radius": 4 * mm});
            skCircle(sketch, "E79.17", {"center": v(-60, 60) * mm, "radius": 4 * mm});
            skCircle(sketch, "E79.18", {"center": v(-60, -60) * mm, "radius": 4 * mm});
            skCircle(sketch, "E79.19", {"center": v(60, -60) * mm, "radius": 4 * mm});
            skLineSegment(sketch, "E80", {"start": v(-33, 74.25) * mm, "end": v(-15, 92.25) * mm});
            skLineSegment(sketch, "E81", {"start": v(-15, 92.25) * mm, "end": v(-15, 104.25) * mm});
            skArc(sketch, "E82", {"start": v(15, 104.25) * mm, "mid": v(0, 119.25) * mm, "end": v(-15, 104.25) * mm});
            skLineSegment(sketch, "E83", {"start": v(15, 104.25) * mm, "end": v(15, 92.25) * mm});
            skLineSegment(sketch, "E84", {"start": v(15, 92.25) * mm, "end": v(33, 74.25) * mm});
            skCircle(sketch, "E85", {"center": v(0, 104.25) * mm, "radius": 6 * mm});
            skLineSegment(sketch, "E86", {"start": v(0, 104.25) * mm, "end": v(0, 74.25) * mm, "construction": true});
            skLineSegment(sketch, "E87", {"start": v(-74.25, 0) * mm, "end": v(74.25, 0) * mm, "construction": true});
            skLineSegment(sketch, "E88.MirrorCS", {"start": v(-15, 92.25) * mm, "end": v(-33, 74.25) * mm});
            skLineSegment(sketch, "E89.MirrorCS", {"start": v(-15, 104.25) * mm, "end": v(-15, 92.25) * mm});
            skLineSegment(sketch, "E90.MirrorCS", {"start": v(33, 74.25) * mm, "end": v(15, 92.25) * mm});
            skLineSegment(sketch, "E91.MirrorCS", {"start": v(15, 92.25) * mm, "end": v(15, 104.25) * mm});
            skArc(sketch, "E92.MirrorCS", {"start": v(-15, 104.25) * mm, "mid": v(0, 119.25) * mm, "end": v(15, 104.25) * mm});
            skLineSegment(sketch, "E93.MirrorCS", {"start": v(74.25, 0) * mm, "end": v(-74.25, 0) * mm, "construction": true});
            skLineSegment(sketch, "E94.MirrorCS", {"start": v(15, -104.25) * mm, "end": v(15, -92.25) * mm});
            skLineSegment(sketch, "E95.MirrorCS", {"start": v(33, -74.25) * mm, "end": v(15, -92.25) * mm});
            skLineSegment(sketch, "E96.MirrorCS", {"start": v(-15, -92.25) * mm, "end": v(-33, -74.25) * mm});
            skLineSegment(sketch, "E97.MirrorCS", {"start": v(-15, -92.25) * mm, "end": v(-15, -104.25) * mm});
            skCircle(sketch, "E98.MirrorC", {"center": v(0, -104.25) * mm, "radius": 6 * mm});
            skLineSegment(sketch, "E99.MirrorCS", {"start": v(0, -104.25) * mm, "end": v(0, -74.25) * mm, "construction": true});
            skArc(sketch, "E100.MirrorCS", {"start": v(15, -104.25) * mm, "mid": v(0, -119.25) * mm, "end": v(-15, -104.25) * mm});
            skSolve(sketch);
        }
        {
            var Q0;
            Q0 = qSketchRegion(id + "F16", true);
            var Q1;
            Q1=makeQuery(id+"F2.opExtrude","CAP_FACE",FACE,{"disambiguationData":[OSD([sQuery(id+"F0.wireOp",EDGE,"E12"),sQuery(id+"F0.wireOp",EDGE,"E13"),sQuery(id+"F0.wireOp",EDGE,"E14"),sQuery(id+"F0.wireOp",EDGE,"E15"),sQuery(id+"F0.wireOp",EDGE,"E17.filletArc"),sQuery(id+"F0.wireOp",EDGE,"E18.filletArc"),sQuery(id+"F0.wireOp",EDGE,"E19.filletArc"),sQuery(id+"F0.wireOp",EDGE,"E20.filletArc"),sQuery(id+"F0.wireOp",EDGE,"E25.0"),sQuery(id+"F0.wireOp",EDGE,"E25.1"),sQuery(id+"F0.wireOp",EDGE,"E25.2"),sQuery(id+"F0.wireOp",EDGE,"E25.3"),sQuery(id+"F0.wireOp",EDGE,"E25.4"),sQuery(id+"F0.wireOp",EDGE,"E25.5"),sQuery(id+"F0.wireOp",EDGE,"E25.6"),sQuery(id+"F0.wireOp",EDGE,"E25.7")])],"isStart":false});
            extrude(context, id + "F17", {"entities" : qUnion([Q0]), "endBound" : BoundingType.UP_TO_SURFACE, "depth" : 25 * mm, "endBoundEntityFace" : qUnion([Q1]), "offsetDistance" : 25 * mm});
        }
    });
